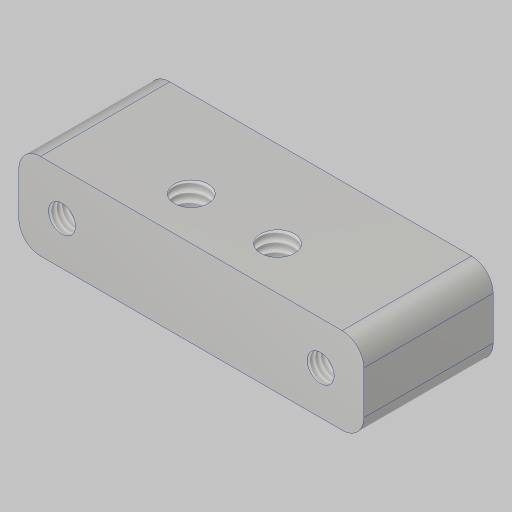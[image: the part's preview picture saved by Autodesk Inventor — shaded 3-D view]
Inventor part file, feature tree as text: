
AUTODESK INVENTOR PART (.ipt)
format: ipt  version: 2023.5 (Build 275446000, 446)  size: 150,016 bytes
history: native  units: in
note: dims shown in document units (in); Inventor stores cm internally (conversion verified against a paired STEP export)
features: sketch x3, hole x2, extrude x1, fillet x1
ambient origin geometry x8: Origin, YZ Plane, XZ Plane, XY Plane, X Axis, Y Axis, Z Axis, Center Point
bodies: Solid1 (feature_tree)
feature tree (7):
  extrude  "Extrusion1"  Depth=0.5in
  hole  "Hole1"  [1 undecoded]
  hole  "Hole2"  [1 undecoded]
  fillet  "Fillet1"  Radius=0.25in
  sketch  "Sketch1"  dims[d0=2.0in d1=0.5in]
  sketch  "Sketch2"  dims[d2=0.75in d3=0.0in d4=0.5in]
  sketch  "Sketch3"  dims[d5=0.196in d6=0.5in d7=0.385in d8=0.25in d9=0.5635in d10=1.0in d11=0.8108in d12=1.5in d13=0.156in d14=0.38in d15=0.375in d16=0.25in d17=0.5635in d18=1.0in d19=0.8108in d20=0.25in d21=0.125in]
note: 2 required parameter values undecoded (feature->parameter linkage not recoverable at this tier; creation-order binding heuristic only, values carry confidence <= 0.55)
